# Revit family: AMZ 112_DN15-50_RFA
name_source: partatom
category: Pipe Accessories
units: mm (PartAtom-declared; Revit-internal decimal feet)

## family parameters
Always vertical = Yes
Cut with Voids When Loaded = No
OmniClass Number = 23.65.55.14.17
OmniClass Title = Adjusting/Controlling Valves for Liquid Services
Part Type = Valve - Breaks Into
Round Connector Dimension = Use Diameter
Shared = No
Work Plane-Based = No

## types (12) — shared parameters
082G1637 = AMZ Actuator_RFA : AMZ 112/113 Actuator_24V_082G1637
082G1638 = AMZ Actuator_RFA : AMZ 112/113 Actuator_230V_082G1638
Connection = Internal thread
Description = Motorized Control Valve
IfcExportAs = IfcValveType
IfcExportType = AMZ 112
LOD 200 = No
LOD 350 = Yes
Manufacturer = Danfoss
Max Medium Temperature = 130 °C
Max Operating Pressure = 6 bar
Min Medium Temperature = 2 °C
Power = 3 VA
Power Consumption = 2.5 VA
URL = https://store.danfoss.com
Valve Body Material = Danfoss Copper Alloy

## per-type parameters (varying)
- AMZ 112_DN15_24V_082G5400: AMZ Actuator=AMZ Actuator_RFA : AMZ 112/113 Actuator_24V_082G1637; D=15 mm  [stored 0.0492126 ft]; H1=29.4 mm; H2=24.4 mm; HS=5 mm  [stored 0.0164042 ft]; Kvs=17.0 m³/h; L1=21 mm  [stored 0.0688976 ft]; L2=15 mm  [stored 0.0492126 ft]; L3=3 mm  [stored 0.00984252 ft]; LS=37.7 mm; Length=61 mm; Model=082G5400; Model Type=AMZ 112_DN15_24V; Nominal Flow (Text)=PN 40; Power Supply=24 VAC; R1=8.5 mm  [stored 0.0278871 ft]; RV1=13.53 mm; RV2=16.5 mm  [stored 0.0541339 ft]; RV3=13.53 mm; Voltage=24 V; WS1=18.5 mm  [stored 0.0606955 ft]; WS2=-18.5 mm  [stored -0.0606955 ft]; W_nut=27 mm  [stored 0.0885827 ft]; Weight=0.93 kg; connector diameter=27.06 mm
- AMZ 112_DN20_24V_082G5401: AMZ Actuator=AMZ Actuator_RFA : AMZ 112/113 Actuator_24V_082G1637; D=20 mm  [stored 0.0656168 ft]; H1=33 mm  [stored 0.108268 ft]; H2=28 mm  [stored 0.0918635 ft]; HS=5 mm  [stored 0.0164042 ft]; Kvs=28.0 m³/h; L1=16.5 mm  [stored 0.0541339 ft]; L2=24.5 mm  [stored 0.0803806 ft]; L3=3 mm  [stored 0.00984252 ft]; LS=37.7 mm; Length=69.5 mm; Model=082G5401; Model Type=AMZ 112_DN20_24V; Nominal Flow (Text)=PN 40; Power Supply=24 VAC; R1=8.5 mm  [stored 0.0278871 ft]; RV1=17 mm; RV2=19.5 mm  [stored 0.0639764 ft]; RV3=17 mm; Voltage=24 V; WS1=18.5 mm  [stored 0.0606955 ft]; WS2=-18.5 mm  [stored -0.0606955 ft]; W_nut=34 mm; Weight=1.04 kg; connector diameter=34 mm
- AMZ 112_DN25_24V_082G5402: AMZ Actuator=AMZ Actuator_RFA : AMZ 112/113 Actuator_24V_082G1637; D=25 mm  [stored 0.082021 ft]; H1=37.2 mm; H2=32.2 mm  [stored 0.105643 ft]; HS=5 mm  [stored 0.0164042 ft]; Kvs=39.0 m³/h; L1=24.2 mm; L2=30.8 mm; L3=3 mm  [stored 0.00984252 ft]; LS=42 mm; Length=84.5 mm; Model=082G5402; Model Type=AMZ 112_DN25_24V; Nominal Flow (Text)=PN 40; Power Supply=24 VAC; R1=9 mm  [stored 0.0295276 ft]; RV1=21.5 mm  [stored 0.0705381 ft]; RV2=24.5 mm  [stored 0.0803806 ft]; RV3=20.7 mm  [stored 0.0679134 ft]; Voltage=24 V; WS1=21 mm  [stored 0.0688976 ft]; WS2=-21 mm  [stored -0.0688976 ft]; W_nut=41.3 mm; Weight=1.26 kg; connector diameter=41.4 mm
- AMZ 112_DN32_24V_082G5403: AMZ Actuator=AMZ Actuator_RFA : AMZ 112/113 Actuator_24V_082G1637; D=32 mm  [stored 0.104987 ft]; H1=47.5 mm; H2=42 mm; HS=5.5 mm  [stored 0.0180446 ft]; Kvs=84.0 m³/h; L1=30 mm  [stored 0.0984252 ft]; L2=26.2 mm  [stored 0.085958 ft]; L3=6 mm  [stored 0.019685 ft]; LS=42 mm; Length=98.5 mm; Model=082G5403; Model Type=AMZ 112_DN32_24V; Nominal Flow (Text)=PN 40; Power Supply=24 VAC; R1=11 mm  [stored 0.0360892 ft]; RV1=25.5 mm; RV2=30 mm  [stored 0.0984252 ft]; RV3=25.5 mm; Voltage=24 V; WS1=21 mm  [stored 0.0688976 ft]; WS2=-21 mm  [stored -0.0688976 ft]; W_nut=51 mm; Weight=1.55 kg; connector diameter=51 mm
- AMZ 112_DN40_24V_082G5404: AMZ Actuator=AMZ Actuator_RFA : AMZ 112/113 Actuator_24V_082G1637; D=40 mm; H1=53 mm; H2=47.5 mm; HS=5.5 mm  [stored 0.0180446 ft]; Kvs=156.0 m³/h; L1=34 mm; L2=25 mm  [stored 0.082021 ft]; L3=5 mm  [stored 0.0164042 ft]; LS=42.3 mm; Length=110 mm; Model=082G5404; Model Type=AMZ 112_DN40_24V; Nominal Flow (Text)=PN 25; Power Supply=24 VAC; R1=11 mm  [stored 0.0360892 ft]; RV1=29.8 mm  [stored 0.097769 ft]; RV2=34.5 mm; RV3=30 mm  [stored 0.0984252 ft]; Voltage=24 V; WS1=21 mm  [stored 0.0688976 ft]; WS2=-21 mm  [stored -0.0688976 ft]; W_nut=60 mm; Weight=1.96 kg; connector diameter=60 mm
- AMZ 112_DN50_24V_082G5405: AMZ Actuator=AMZ Actuator_RFA : AMZ 112/113 Actuator_24V_082G1637; D=50 mm; H1=64 mm; H2=58.5 mm; HS=5.5 mm  [stored 0.0180446 ft]; Kvs=243.0 m³/h; L1=32.5 mm  [stored 0.106627 ft]; L2=41.5 mm; L3=3 mm  [stored 0.00984252 ft]; LS=48.2 mm; Length=130 mm; Model=082G5405; Model Type=AMZ 112_DN50_24V; Nominal Flow (Text)=PN 25; Power Supply=24 VAC; R1=13 mm; RV1=39.5 mm; RV2=42.5 mm; RV3=37 mm; Voltage=24 V; WS1=24 mm  [stored 0.0787402 ft]; WS2=-24 mm  [stored -0.0787402 ft]; W_nut=74 mm; Weight=2.78 kg; connector diameter=74 mm
- AMZ 112_DN15_230V_082G5406: AMZ Actuator=AMZ Actuator_RFA : AMZ 112/113 Actuator_230V_082G1638; D=15 mm  [stored 0.0492126 ft]; H1=29.4 mm; H2=24.4 mm; HS=5 mm  [stored 0.0164042 ft]; Kvs=17.0 m³/h; L1=21 mm  [stored 0.0688976 ft]; L2=15 mm  [stored 0.0492126 ft]; L3=3 mm  [stored 0.00984252 ft]; LS=37.7 mm; Length=61 mm; Model=082G5406; Model Type=AMZ 112_DN15_230V; Nominal Flow (Text)=PN 40; Power Supply=230 VAC; R1=8.5 mm  [stored 0.0278871 ft]; RV1=13.53 mm; RV2=16.5 mm  [stored 0.0541339 ft]; RV3=13.53 mm; Voltage=230 V; WS1=18.5 mm  [stored 0.0606955 ft]; WS2=-18.5 mm  [stored -0.0606955 ft]; W_nut=27 mm  [stored 0.0885827 ft]; Weight=0.83 kg; connector diameter=27.06 mm
- AMZ 112_DN20_230V_082G5407: AMZ Actuator=AMZ Actuator_RFA : AMZ 112/113 Actuator_230V_082G1638; D=20 mm  [stored 0.0656168 ft]; H1=33 mm  [stored 0.108268 ft]; H2=28 mm  [stored 0.0918635 ft]; HS=5 mm  [stored 0.0164042 ft]; Kvs=28.0 m³/h; L1=16.5 mm  [stored 0.0541339 ft]; L2=24.5 mm  [stored 0.0803806 ft]; L3=3 mm  [stored 0.00984252 ft]; LS=37.7 mm; Length=69.5 mm; Model=082G5407; Model Type=AMZ 112_DN20_230V; Nominal Flow (Text)=PN 40; Power Supply=230 VAC; R1=8.5 mm  [stored 0.0278871 ft]; RV1=17 mm; RV2=19.5 mm  [stored 0.0639764 ft]; RV3=17 mm; Voltage=230 V; WS1=18.5 mm  [stored 0.0606955 ft]; WS2=-18.5 mm  [stored -0.0606955 ft]; W_nut=34 mm; Weight=0.93 kg; connector diameter=34 mm
- AMZ 112_DN25_230V_082G5408: AMZ Actuator=AMZ Actuator_RFA : AMZ 112/113 Actuator_230V_082G1638; D=25 mm  [stored 0.082021 ft]; H1=37.2 mm; H2=32.2 mm  [stored 0.105643 ft]; HS=5 mm  [stored 0.0164042 ft]; Kvs=39.0 m³/h; L1=24.2 mm; L2=30.8 mm; L3=3 mm  [stored 0.00984252 ft]; LS=42 mm; Length=84.5 mm; Model=082G5408; Model Type=AMZ 112_DN25_230V; Nominal Flow (Text)=PN 40; Power Supply=230 VAC; R1=9 mm  [stored 0.0295276 ft]; RV1=21.5 mm  [stored 0.0705381 ft]; RV2=24.5 mm  [stored 0.0803806 ft]; RV3=20.7 mm  [stored 0.0679134 ft]; Voltage=230 V; WS1=21 mm  [stored 0.0688976 ft]; WS2=-21 mm  [stored -0.0688976 ft]; W_nut=41.3 mm; Weight=0.00 kg; connector diameter=41.4 mm
- AMZ 112_DN32_230V_082G5409: AMZ Actuator=AMZ Actuator_RFA : AMZ 112/113 Actuator_230V_082G1638; D=32 mm  [stored 0.104987 ft]; H1=47.5 mm; H2=42 mm; HS=5.5 mm  [stored 0.0180446 ft]; Kvs=84.0 m³/h; L1=30 mm  [stored 0.0984252 ft]; L2=26.2 mm  [stored 0.085958 ft]; L3=6 mm  [stored 0.019685 ft]; LS=42 mm; Length=98.5 mm; Model=082G5409; Model Type=AMZ 112_DN32_230V; Nominal Flow (Text)=PN 40; Power Supply=230 VAC; R1=11 mm  [stored 0.0360892 ft]; RV1=25.5 mm; RV2=30 mm  [stored 0.0984252 ft]; RV3=25.5 mm; Voltage=230 V; WS1=21 mm  [stored 0.0688976 ft]; WS2=-21 mm  [stored -0.0688976 ft]; W_nut=51 mm; Weight=1.64 kg; connector diameter=51 mm
- AMZ 112_DN40_230V_082G5410: AMZ Actuator=AMZ Actuator_RFA : AMZ 112/113 Actuator_230V_082G1638; D=40 mm; H1=53 mm; H2=47.5 mm; HS=5.5 mm  [stored 0.0180446 ft]; Kvs=156.0 m³/h; L1=34 mm; L2=25 mm  [stored 0.082021 ft]; L3=5 mm  [stored 0.0164042 ft]; LS=42.3 mm; Length=110 mm; Model=082G5410; Model Type=AMZ 112_DN40_230V; Nominal Flow (Text)=PN 25; Power Supply=230 VAC; R1=11 mm  [stored 0.0360892 ft]; RV1=29.8 mm  [stored 0.097769 ft]; RV2=34.5 mm; RV3=30 mm  [stored 0.0984252 ft]; Voltage=230 V; WS1=21 mm  [stored 0.0688976 ft]; WS2=-21 mm  [stored -0.0688976 ft]; W_nut=60 mm; Weight=1.95 kg; connector diameter=60 mm
- AMZ 112_DN50_230V_082G5411: AMZ Actuator=AMZ Actuator_RFA : AMZ 112/113 Actuator_230V_082G1638; D=50 mm; H1=64 mm; H2=58.5 mm; HS=5.5 mm  [stored 0.0180446 ft]; Kvs=243.0 m³/h; L1=32.5 mm  [stored 0.106627 ft]; L2=41.5 mm; L3=3 mm  [stored 0.00984252 ft]; LS=48.2 mm; Length=130 mm; Model=082G5411; Model Type=AMZ 112_DN50_230V; Nominal Flow (Text)=PN 25; Power Supply=230 VAC; R1=13 mm; RV1=39.5 mm; RV2=42.5 mm; RV3=37 mm; Voltage=230 V; WS1=24 mm  [stored 0.0787402 ft]; WS2=-24 mm  [stored -0.0787402 ft]; W_nut=74 mm; Weight=2.77 kg; connector diameter=74 mm

note: [stored X ft] marks values corroborated as IEEE doubles in the binary element streams (Revit-internal decimal feet)

## geometry (parser evidence)
native form markers: Sweep x6
no freeform markers — native parametric forms only
